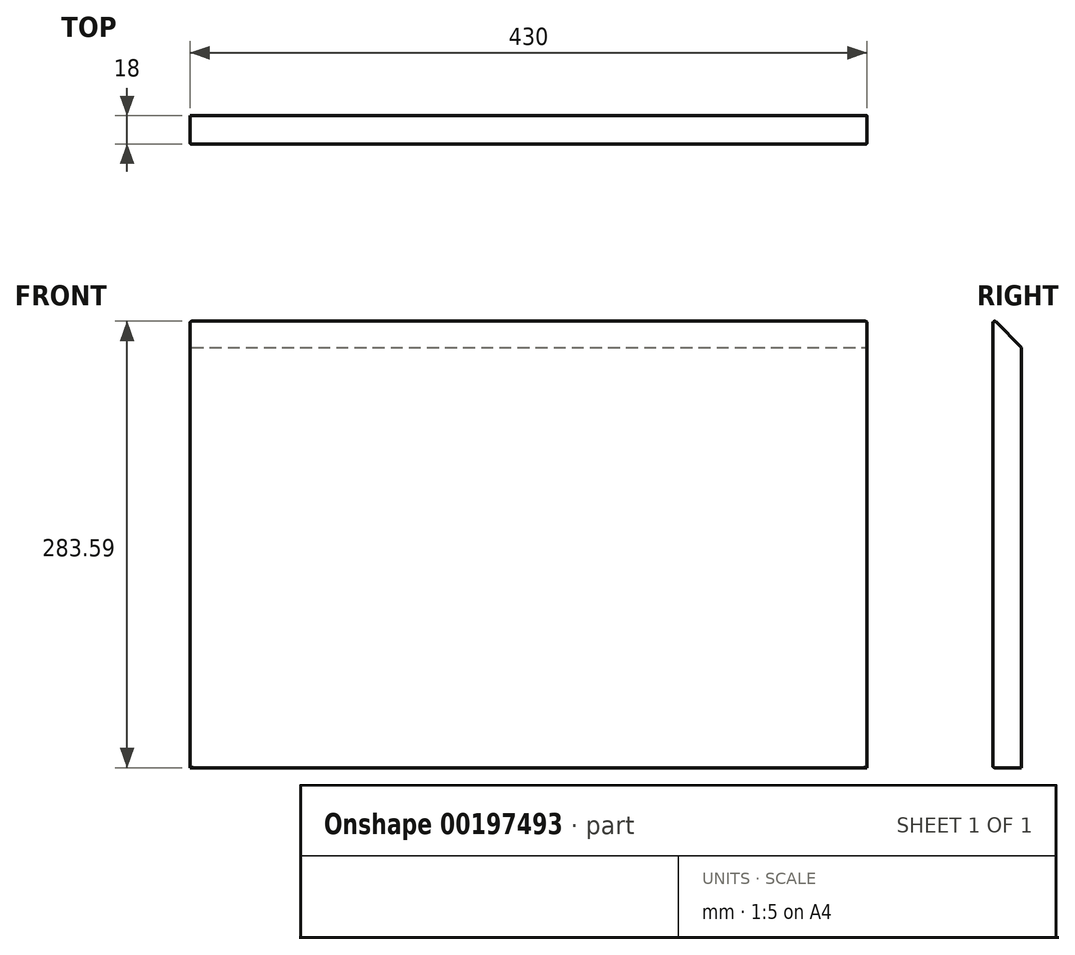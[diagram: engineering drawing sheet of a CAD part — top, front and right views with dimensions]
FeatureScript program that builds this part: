
annotation { "Feature Type Name" : "Feature", "Feature Type Description" : "" }
export const myFeature = defineFeature(function(context is Context, id is Id, definition is map)
    precondition{}
    {
        {
            var Q0;
            Q0=qCreatedBy(makeId("Front.planeOp"),FACE);
            var sketch = newSketch(context, id + "F0", { "sketchPlane" : qUnion([Q0])});
            skLineSegment(sketch, "E0.bottom", {"start": v(-215, 142.5) * mm, "end": v(215, 142.5) * mm});
            skLineSegment(sketch, "E0.top", {"start": v(-215, -142.5) * mm, "end": v(215, -142.5) * mm});
            skLineSegment(sketch, "E0.left", {"start": v(-215, 142.5) * mm, "end": v(-215, -142.5) * mm});
            skLineSegment(sketch, "E0.right", {"start": v(215, 142.5) * mm, "end": v(215, -142.5) * mm});
            skPoint(sketch, "E0.middle", {"position": v(0, 0) * mm});
            skSolve(sketch);
        }
        {
            var Q0;
            Q0 = qSketchRegion(id + "F0", true);
            extrude(context, id + "F1", {"entities" : qUnion([Q0]), "depth" : 18 * mm});
        }
        {
            var Q0;
            Q0=makeQuery(id+"F1.opExtrude","SWEPT_FACE",FACE,{"disambiguationData":[OSD([sQuery(id+"F0.wireOp",EDGE,"E0.right")])]});
            var sketch = newSketch(context, id + "F2", { "sketchPlane" : qUnion([Q0])});
            skLineSegment(sketch, "E1", {"start": v(-18, 142.5) * mm, "end": v(0, 142.5) * mm});
            skLineSegment(sketch, "E2", {"start": v(0, 142.5) * mm, "end": v(0, 124.5) * mm});
            skLineSegment(sketch, "E3", {"start": v(0, 124.5) * mm, "end": v(-18, 142.5) * mm});
            skSolve(sketch);
        }
        {
            var Q0;
            Q0 = qSketchRegion(id + "F2", true);
            extrude(context, id + "F3", {"entities" : qUnion([Q0]), "operationType" : NewBodyOperationType.REMOVE, "oppositeDirection" : true, "depth" : 438 * mm});
        }
        {
            var Q0;
            Q0=makeQuery(id+"F3.boolean.opBoolean","MERGE",EDGE,{"derivedFrom":[makeQuery(id+"F1.opExtrude","CAP_EDGE",EDGE,{"disambiguationData":[OSD([sQuery(id+"F0.wireOp",EDGE,"E0.bottom")])],"isStart":false}),makeQuery(id+"F3.opExtrude","SWEPT_EDGE",EDGE,{"disambiguationData":[OSD([sQuery(id+"F0.wireOp",EDGE,"E0.right"),sQuery(id+"F2.wireOp",EDGE,"E1"),sQuery(id+"F2.wireOp",EDGE,"E3")])]})]});
            fillet(context, id + "F4", {"entities" : qUnion([Q0]), "radius" : 1 * mm, "tangentPropagation" : true, "allowEdgeOverflow" : false});
        }
        {
            var Q0;
            Q0=makeQuery(id+"F1.opExtrude","CAP_EDGE",EDGE,{"disambiguationData":[OSD([sQuery(id+"F0.wireOp",EDGE,"E0.left")])],"isStart":false});
            var Q1;
            Q1=makeQuery(id+"F1.opExtrude","CAP_EDGE",EDGE,{"disambiguationData":[OSD([sQuery(id+"F0.wireOp",EDGE,"E0.top")])],"isStart":false});
            var Q2;
            Q2=makeQuery(id+"F1.opExtrude","CAP_EDGE",EDGE,{"disambiguationData":[OSD([sQuery(id+"F0.wireOp",EDGE,"E0.right")])],"isStart":false});
            fillet(context, id + "F5", {"entities" : qUnion([Q0, Q1, Q2]), "radius" : 1 * mm, "tangentPropagation" : true, "allowEdgeOverflow" : false});
        }
    });
